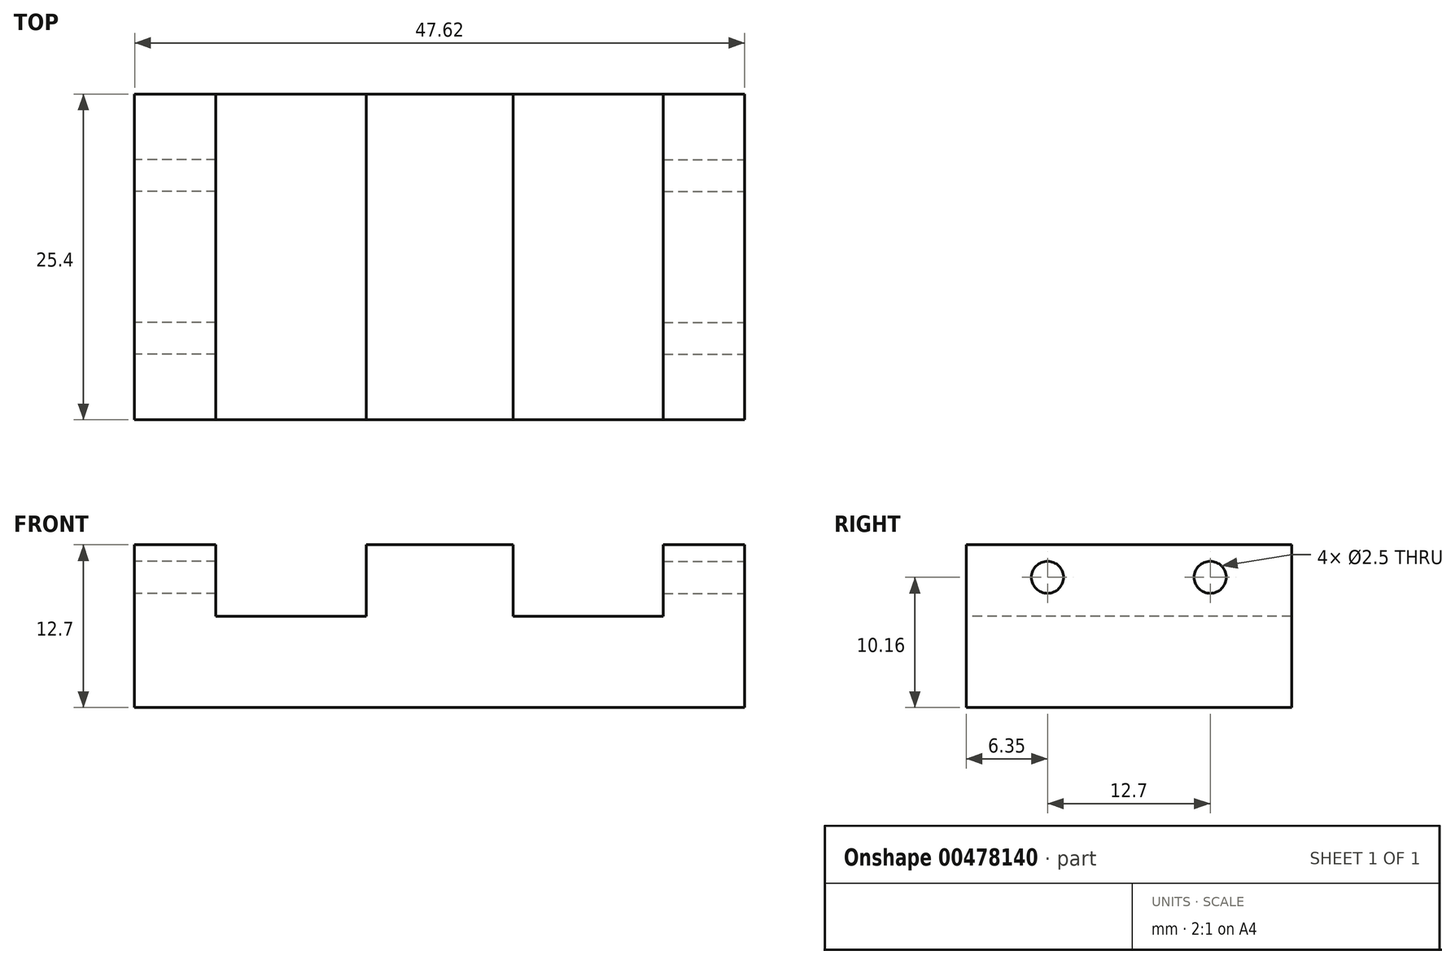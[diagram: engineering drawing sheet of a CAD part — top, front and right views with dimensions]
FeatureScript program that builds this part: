
annotation { "Feature Type Name" : "Feature", "Feature Type Description" : "" }
export const myFeature = defineFeature(function(context is Context, id is Id, definition is map)
    precondition{}
    {
        {
            var Q0;
            Q0=qCreatedBy(makeId("Top.planeOp"),FACE);
            var sketch = newSketch(context, id + "F0", { "sketchPlane" : qUnion([Q0])});
            skLineSegment(sketch, "E0.bottom", {"start": v(23.81, 12.7) * mm, "end": v(-23.81, 12.7) * mm});
            skLineSegment(sketch, "E0.top", {"start": v(23.81, -12.7) * mm, "end": v(-23.81, -12.7) * mm});
            skLineSegment(sketch, "E0.left", {"start": v(23.81, 12.7) * mm, "end": v(23.81, -12.7) * mm});
            skLineSegment(sketch, "E0.right", {"start": v(-23.81, 12.7) * mm, "end": v(-23.81, -12.7) * mm});
            skPoint(sketch, "E0.middle", {"position": v(0, 0) * mm});
            skSolve(sketch);
        }
        {
            var Q0;
            Q0=makeQuery(id+"F0.imprint","IMPRINT",FACE,{"disambiguationData":[TD([[makeQuery(id+"F0.imprint","IMPRINT",EDGE,{"derivedFrom":sQuery(id+"F0.wireOp",EDGE,"E0.bottom")}),1.0]])]});
            extrude(context, id + "F1", {"entities" : qUnion([Q0]), "depth" : 12.7 * mm});
        }
        {
            var Q0;
            Q0=makeQuery(id+"F1.opExtrude","CAP_FACE",FACE,{"disambiguationData":[OSD([sQuery(id+"F0.wireOp",EDGE,"E0.bottom"),sQuery(id+"F0.wireOp",EDGE,"E0.top"),sQuery(id+"F0.wireOp",EDGE,"E0.left"),sQuery(id+"F0.wireOp",EDGE,"E0.right")])],"isStart":false});
            var sketch = newSketch(context, id + "F2", { "sketchPlane" : qUnion([Q0])});
            skLineSegment(sketch, "E1.bottom", {"start": v(-17.46, 12.7) * mm, "end": v(-5.73, 12.7) * mm});
            skLineSegment(sketch, "E1.top", {"start": v(-17.46, -12.7) * mm, "end": v(-5.73, -12.7) * mm});
            skLineSegment(sketch, "E1.left", {"start": v(-17.46, 12.7) * mm, "end": v(-17.46, -12.7) * mm});
            skLineSegment(sketch, "E1.right", {"start": v(-5.73, 12.7) * mm, "end": v(-5.73, -12.7) * mm});
            skLineSegment(sketch, "E2.MirrorCS", {"start": v(5.73, 12.7) * mm, "end": v(5.73, -12.7) * mm});
            skLineSegment(sketch, "E3.MirrorCS", {"start": v(17.46, 12.7) * mm, "end": v(17.46, -12.7) * mm});
            skLineSegment(sketch, "E4.MirrorCS", {"start": v(17.46, -12.7) * mm, "end": v(5.73, -12.7) * mm});
            skLineSegment(sketch, "E5.MirrorCS", {"start": v(17.46, 12.7) * mm, "end": v(5.73, 12.7) * mm});
            skSolve(sketch);
        }
        {
            var Q0;
            Q0=makeQuery(id+"F2.imprint","IMPRINT",FACE,{"disambiguationData":[TD([[makeQuery(id+"F2.imprint","IMPRINT",EDGE,{"derivedFrom":sQuery(id+"F2.wireOp",EDGE,"E1.bottom")}),1.0]])]});
            var Q1;
            Q1=makeQuery(id+"F2.imprint","IMPRINT",FACE,{"disambiguationData":[TD([[makeQuery(id+"F2.imprint","IMPRINT",EDGE,{"derivedFrom":sQuery(id+"F2.wireOp",EDGE,"E2.MirrorCS")}),1.0]])]});
            extrude(context, id + "F3", {"entities" : qUnion([Q0, Q1]), "operationType" : NewBodyOperationType.REMOVE, "oppositeDirection" : true, "depth" : 5.6 * mm});
        }
        {
            var Q0;
            Q0=makeQuery(id+"F1.opExtrude","SWEPT_FACE",FACE,{"disambiguationData":[OSD([sQuery(id+"F0.wireOp",EDGE,"E0.right")])]});
            var sketch = newSketch(context, id + "F4", { "sketchPlane" : qUnion([Q0])});
            skPoint(sketch, "E6", {"position": v(-6.35, 10.16) * mm});
            skPoint(sketch, "E7.MirrorP", {"position": v(6.35, 10.16) * mm});
            skSolve(sketch);
        }
        {
            var Q0;
            Q0=makeQuery(id+"F1.opExtrude","SWEPT_FACE",FACE,{"disambiguationData":[OSD([sQuery(id+"F0.wireOp",EDGE,"E0.left")])]});
            var sketch = newSketch(context, id + "F5", { "sketchPlane" : qUnion([Q0])});
            skPoint(sketch, "E8", {"position": v(-6.35, 10.16) * mm});
            skPoint(sketch, "E9.MirrorP", {"position": v(6.35, 10.16) * mm});
            skSolve(sketch);
        }
        {
            var Q0;
            Q0=sQuery(id+"F4.wireOp",VERTEX,"E7.MirrorP");
            var Q1;
            Q1=sQuery(id+"F4.wireOp",VERTEX,"E6");
            var Q2;
            Q2=makeQuery(id+"F1.opExtrude","SWEPT_BODY",BODY,{"disambiguationData":[OSD([sQuery(id+"F0.wireOp",EDGE,"E0.bottom"),sQuery(id+"F0.wireOp",EDGE,"E0.top"),sQuery(id+"F0.wireOp",EDGE,"E0.left"),sQuery(id+"F0.wireOp",EDGE,"E0.right")])]});
            hole(context, id + "F6", {"style" : HoleStyle.SIMPLE, "endStyle" : HoleEndStyle.BLIND, "standardTappedOrClearance" : lookupTablePath({ "standard" : "ISO", "engagement" : "75%", "pitch" : "0.5 mm", "size" : "M3", "type" : "Tapped" }), "standardBlindInLast" : lookupTablePath({ "standard" : "ISO", "engagement" : "75%", "pitch" : "0.5 mm", "size" : "M3", "type" : "Tapped" }), "holeDiameter" : 2.5 * mm, "showTappedDepth" : true, "holeDepth" : 7.62 * mm, "isTappedThrough" : true, "tappedDepth" : 3.62 * mm, "tapClearance" : 8, "startFromSketch" : true, "locations" : qUnion([Q0, Q1]), "scope" : qUnion([Q2]), "majorDiameter" : 3 * mm});
        }
        {
            var Q0;
            Q0=sQuery(id+"F5.wireOp",VERTEX,"E8");
            var Q1;
            Q1=sQuery(id+"F5.wireOp",VERTEX,"E9.MirrorP");
            var Q2;
            Q2=makeQuery(id+"F1.opExtrude","SWEPT_BODY",BODY,{"disambiguationData":[OSD([sQuery(id+"F0.wireOp",EDGE,"E0.bottom"),sQuery(id+"F0.wireOp",EDGE,"E0.top"),sQuery(id+"F0.wireOp",EDGE,"E0.left"),sQuery(id+"F0.wireOp",EDGE,"E0.right")])]});
            hole(context, id + "F7", {"style" : HoleStyle.SIMPLE, "endStyle" : HoleEndStyle.BLIND, "standardTappedOrClearance" : lookupTablePath({ "standard" : "ISO", "engagement" : "75%", "pitch" : "0.5 mm", "size" : "M3", "type" : "Tapped" }), "standardBlindInLast" : lookupTablePath({ "standard" : "ISO", "engagement" : "75%", "pitch" : "0.5 mm", "size" : "M3", "type" : "Tapped" }), "holeDiameter" : 2.5 * mm, "showTappedDepth" : true, "holeDepth" : 7.62 * mm, "isTappedThrough" : true, "tappedDepth" : 3.62 * mm, "tapClearance" : 8, "startFromSketch" : true, "locations" : qUnion([Q0, Q1]), "scope" : qUnion([Q2]), "majorDiameter" : 3 * mm});
        }
    });
